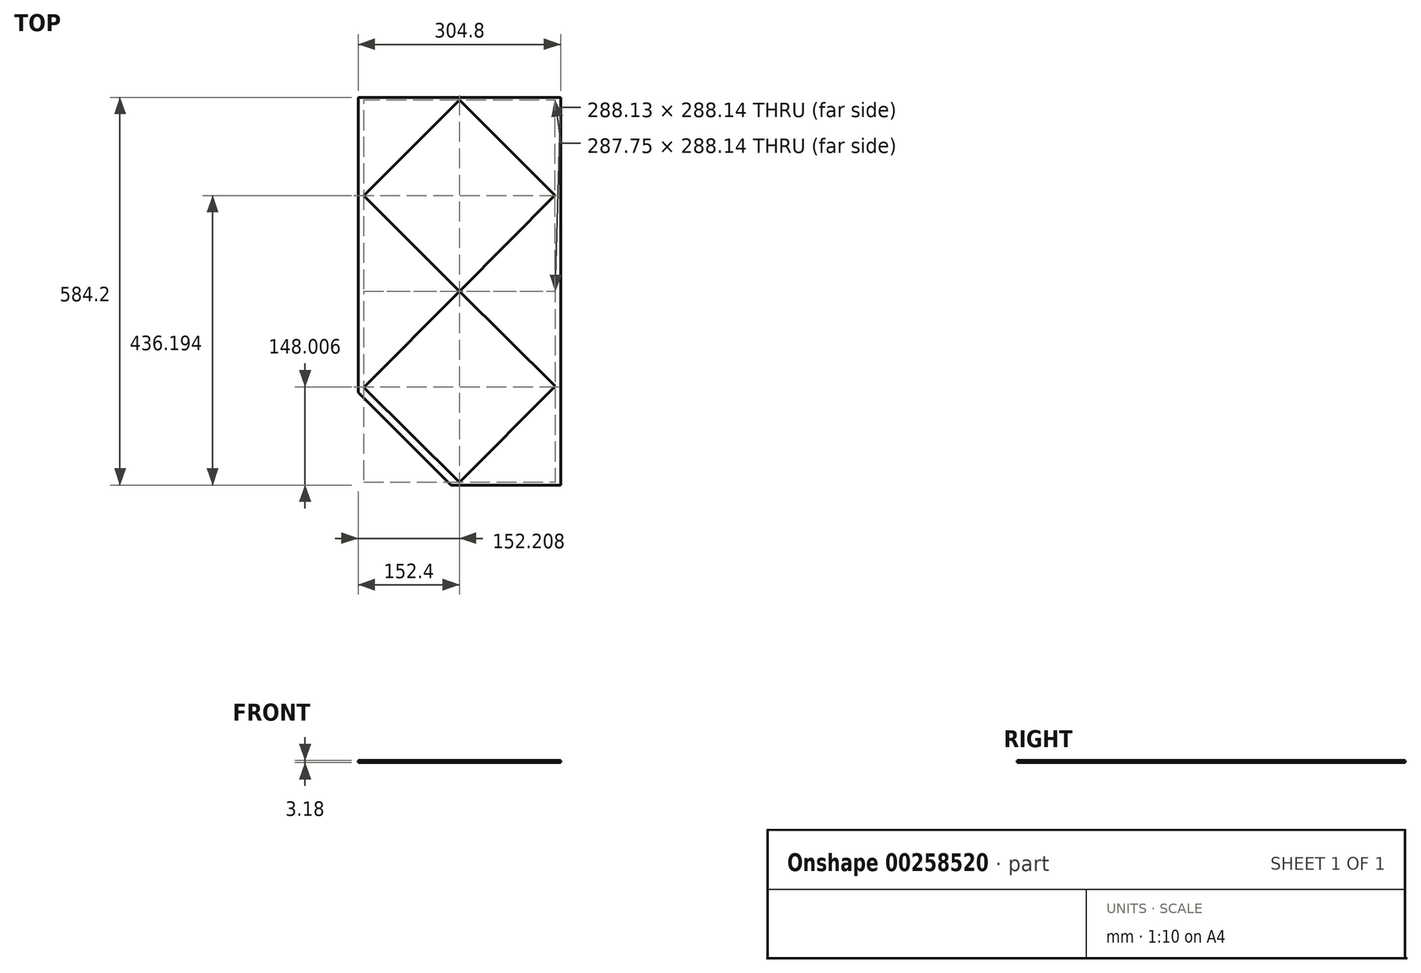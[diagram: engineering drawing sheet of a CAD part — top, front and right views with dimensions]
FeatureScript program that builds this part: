
annotation { "Feature Type Name" : "Feature", "Feature Type Description" : "" }
export const myFeature = defineFeature(function(context is Context, id is Id, definition is map)
    precondition{}
    {
        {
            var Q0;
            Q0=qCreatedBy(makeId("Top.planeOp"),FACE);
            var sketch = newSketch(context, id + "F0", { "sketchPlane" : qUnion([Q0])});
            skLineSegment(sketch, "E0.bottom", {"start": v(152.4, 292.1) * mm, "end": v(-152.4, 292.1) * mm});
            skLineSegment(sketch, "E0.top", {"start": v(12.7, -292.1) * mm, "end": v(-12.7, -292.1) * mm});
            skLineSegment(sketch, "E0.left", {"start": v(152.4, 292.1) * mm, "end": v(152.4, -152.4) * mm});
            skLineSegment(sketch, "E0.right", {"start": v(-152.4, 292.1) * mm, "end": v(-152.4, -152.4) * mm});
            skPoint(sketch, "E0.middle", {"position": v(0, 0) * mm});
            skPoint(sketch, "E1.orphan", {"position": v(152.4, -292.1) * mm});
            skLineSegment(sketch, "E2", {"start": v(12.7, -292.1) * mm, "end": v(152.4, -292.1) * mm});
            skLineSegment(sketch, "E3", {"start": v(152.4, -152.4) * mm, "end": v(152.4, -292.1) * mm});
            skLineSegment(sketch, "E4", {"start": v(-152.4, -152.4) * mm, "end": v(-12.7, -292.1) * mm});
            skPoint(sketch, "E5.orphan", {"position": v(-152.4, -292.1) * mm});
            skSolve(sketch);
        }
        {
            var Q0;
            Q0=qSketchRegion(id+"F0",true);
            extrude(context, id + "F1", {"entities" : qUnion([Q0]), "depth" : 3.17 * mm});
        }
        {
            var Q0;
            Q0=makeQuery(id+"F1.opExtrude","CAP_FACE",FACE,{"disambiguationData":[OSD([sQuery(id+"F0.wireOp",EDGE,"E0.bottom"),sQuery(id+"F0.wireOp",EDGE,"E0.top"),sQuery(id+"F0.wireOp",EDGE,"E0.left"),sQuery(id+"F0.wireOp",EDGE,"E0.right"),sQuery(id+"F0.wireOp",EDGE,"XXwYg06J-Xx4f-yiAU-ntJm-qOcsEpnRRI2s")])],"isStart":false});
            var sketch = newSketch(context, id + "F2", { "sketchPlane" : qUnion([Q0])});
            skLineSegment(sketch, "E6", {"start": v(-141.82, 146.34) * mm, "end": v(-2.25, 285.92) * mm});
            skLineSegment(sketch, "E7", {"start": v(2.25, 285.92) * mm, "end": v(141.45, 146.72) * mm});
            skLineSegment(sketch, "E8", {"start": v(-141.82, -147.1) * mm, "end": v(-2.25, -285.92) * mm});
            skLineSegment(sketch, "E9", {"start": v(2.24, -285.91) * mm, "end": v(141.83, -145.58) * mm});
            skPoint(sketch, "E10.end.orphan", {"position": v(0, 0) * mm});
            skLineSegment(sketch, "E11", {"start": v(-141.83, -142.6) * mm, "end": v(-2.24, -2.28) * mm});
            skLineSegment(sketch, "E12", {"start": v(2.25, -2.26) * mm, "end": v(141.82, -141.09) * mm});
            skLineSegment(sketch, "E13", {"start": v(-141.82, 141.85) * mm, "end": v(-2.25, 2.28) * mm});
            skLineSegment(sketch, "E14", {"start": v(2.25, 2.28) * mm, "end": v(141.45, 142.23) * mm});
            skPoint(sketch, "E15.visualSharp", {"position": v(0, 288.16) * mm});
            skArc(sketch, "E15.filletArc", {"start": v(2.25, 285.92) * mm, "mid": v(0, 286.85) * mm, "end": v(-2.25, 285.92) * mm});
            skPoint(sketch, "E16.visualSharp", {"position": v(-144.07, 144.1) * mm});
            skArc(sketch, "E16.filletArc", {"start": v(-141.82, 146.34) * mm, "mid": v(-142.75, 144.1) * mm, "end": v(-141.82, 141.85) * mm});
            skPoint(sketch, "E17.visualSharp", {"position": v(143.68, 144.48) * mm});
            skArc(sketch, "E17.filletArc", {"start": v(141.45, 142.23) * mm, "mid": v(142.37, 144.48) * mm, "end": v(141.45, 146.72) * mm});
            skPoint(sketch, "E18.visualSharp", {"position": v(0, 0.03) * mm});
            skArc(sketch, "E18.filletArc", {"start": v(-2.25, 2.28) * mm, "mid": v(0, 1.35) * mm, "end": v(2.25, 2.28) * mm});
            skPoint(sketch, "E19.visualSharp", {"position": v(0, -0.03) * mm});
            skArc(sketch, "E19.filletArc", {"start": v(2.25, -2.26) * mm, "mid": v(0, -1.34) * mm, "end": v(-2.24, -2.28) * mm});
            skPoint(sketch, "E20.visualSharp", {"position": v(-144.07, -144.86) * mm});
            skArc(sketch, "E20.filletArc", {"start": v(-141.83, -142.6) * mm, "mid": v(-142.75, -144.86) * mm, "end": v(-141.82, -147.1) * mm});
            skPoint(sketch, "E21.visualSharp", {"position": v(144.07, -143.33) * mm});
            skArc(sketch, "E21.filletArc", {"start": v(141.83, -145.58) * mm, "mid": v(142.75, -143.33) * mm, "end": v(141.82, -141.09) * mm});
            skPoint(sketch, "E22.visualSharp", {"position": v(0, -288.16) * mm});
            skArc(sketch, "E22.filletArc", {"start": v(-2.25, -285.92) * mm, "mid": v(0, -286.85) * mm, "end": v(2.24, -285.91) * mm});
            skLineSegment(sketch, "E23", {"start": v(-141.82, 146.34) * mm, "end": v(-144.07, 144.1) * mm});
            skLineSegment(sketch, "E24", {"start": v(-141.82, 141.85) * mm, "end": v(-144.07, 144.1) * mm});
            skLineSegment(sketch, "E25", {"start": v(-2.25, 285.92) * mm, "end": v(0, 288.16) * mm});
            skLineSegment(sketch, "E26", {"start": v(2.25, 285.92) * mm, "end": v(0, 288.16) * mm});
            skLineSegment(sketch, "E27", {"start": v(141.45, 146.72) * mm, "end": v(143.68, 144.48) * mm});
            skLineSegment(sketch, "E28", {"start": v(143.68, 144.48) * mm, "end": v(141.45, 142.23) * mm});
            skLineSegment(sketch, "E29", {"start": v(-144.07, -144.86) * mm, "end": v(-141.83, -142.6) * mm});
            skLineSegment(sketch, "E30", {"start": v(-144.07, -144.86) * mm, "end": v(-141.82, -147.1) * mm});
            skLineSegment(sketch, "E31", {"start": v(-2.25, -285.92) * mm, "end": v(0, -288.16) * mm});
            skLineSegment(sketch, "E32", {"start": v(2.24, -285.91) * mm, "end": v(0, -288.16) * mm});
            skLineSegment(sketch, "E33", {"start": v(141.82, -141.09) * mm, "end": v(144.07, -143.33) * mm});
            skLineSegment(sketch, "E34", {"start": v(141.83, -145.58) * mm, "end": v(144.07, -143.33) * mm});
            skLineSegment(sketch, "E35", {"start": v(-2.24, -2.28) * mm, "end": v(0, -0.03) * mm});
            skLineSegment(sketch, "E36", {"start": v(2.25, -2.26) * mm, "end": v(0, -0.03) * mm});
            skLineSegment(sketch, "E37", {"start": v(0, 0.03) * mm, "end": v(-2.25, 2.28) * mm});
            skLineSegment(sketch, "E38", {"start": v(0, 0.03) * mm, "end": v(2.25, 2.28) * mm});
            skSolve(sketch);
        }
        {
            var Q0;
            Q0=qSketchRegion(id+"F2",true);
            extrude(context, id + "F3", {"entities" : qUnion([Q0]), "operationType" : NewBodyOperationType.REMOVE, "oppositeDirection" : true, "depth" : 25.4 * mm});
        }
    });
